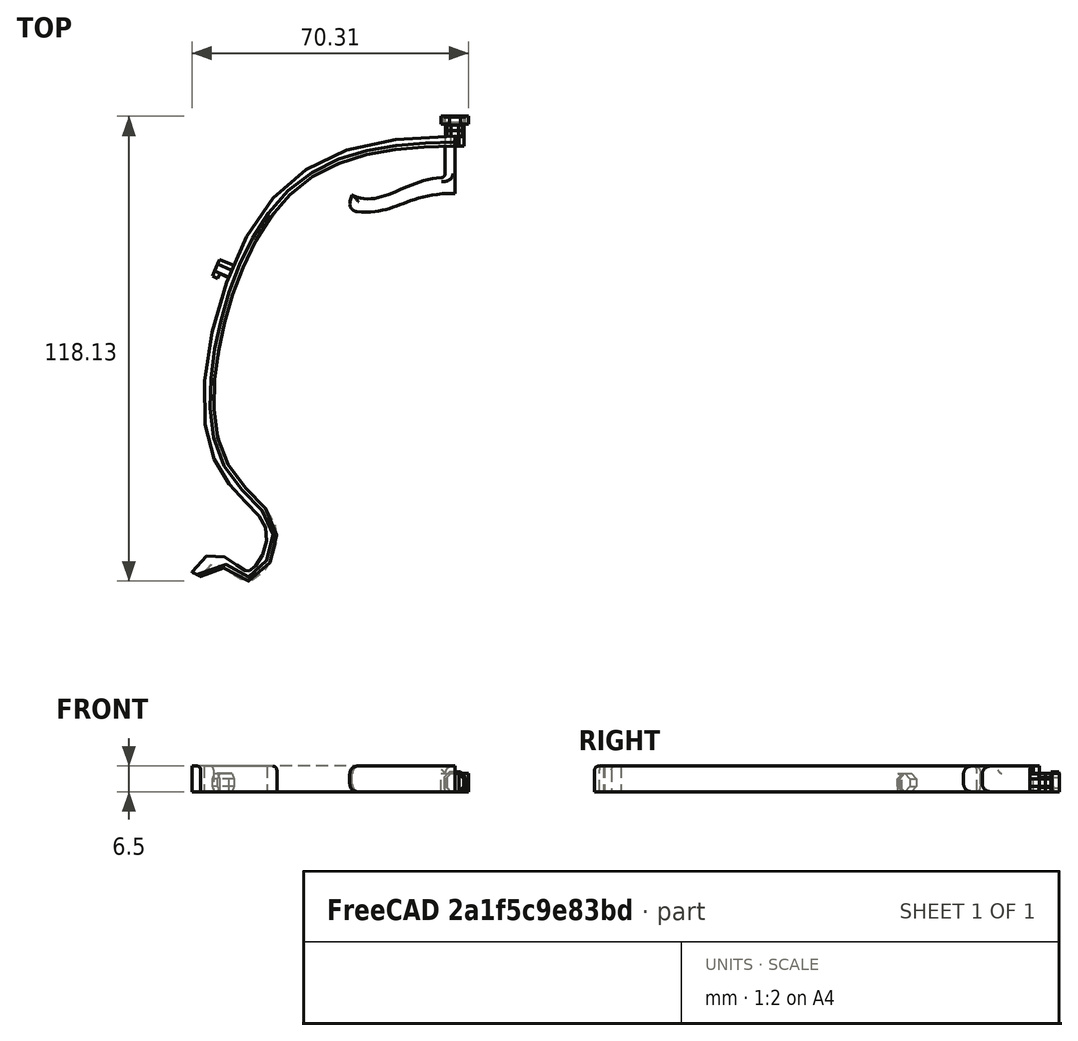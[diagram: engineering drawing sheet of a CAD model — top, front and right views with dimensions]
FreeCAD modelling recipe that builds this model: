
FCSTD DOCUMENT  (FreeCAD 0.18R16146 (Git))
Label: frame-001-02
License: All rights reserved
LicenseURL: http://ja.wikipedia.org/wiki/%E8%91%97%E4%BD%9C%E6%A8%A9%E8%A1%A8%E7%A4%BA
objects: Sketcher::SketchObject×5, Part::Extrusion×5, Part::Box×3, Part::Cut×2, Part::Fillet×2, Part::Compound×2, Mesh::Feature×1, Part::Sweep×1, Part::Mirroring×1, Part::MultiCommon×1
note: 22 computed .brp shape members not serialized (recipe doc carries the construction recipe); baked Part::Feature solids carry a one-line shape summary decoded from their .brp

FEATURE [Sketcher::SketchObject] Sketch  label="Sketch_FrameShape"
  sketch-geometry (15):
    g0-g7: Circle [constr] x8 (B-spline internal-alignment scaffolding for g8; pole/knot coordinates omitted)
    g8: BSplineCurve PolesCount=8 KnotsCount=6 Degree=3 IsPeriodic=0
    g9-g14: GeomPoint [constr] x6 (B-spline internal-alignment scaffolding for g8; pole/knot coordinates omitted)
  constraints (6):
    c: Radius(g0) = 6
    c: Equal(g0, g1-g6) x6
    c: InternalAlignment(g0-g7 -> g8) x8
    c: InternalAlignment(g9-g14 -> g8) x6
    c: Horizontal(g1,g8)
    c: Coincident(g-1,g8)
FEATURE [Sketcher::SketchObject] Sketch001
  Placement = pos=(0,0,0) rot=(0.57735,0.57735,0.57735;2.0944rad)
  sketch-geometry (4):
    g0: LineSegment StartX=0 StartY=6.5 StartZ=0 EndX=2.5 EndY=6.5 EndZ=0
    g1: LineSegment StartX=2.5 StartY=6.5 StartZ=0 EndX=2.5 EndY=0 EndZ=0
    g2: LineSegment StartX=2.5 StartY=0 StartZ=0 EndX=0 EndY=0 EndZ=0
    g3: LineSegment StartX=0 StartY=0 StartZ=0 EndX=0 EndY=6.5 EndZ=0
  constraints (12):
    c: Coincident(g0,g1)
    c: Coincident(g1,g2)
    c: Coincident(g2,g3)
    c: Coincident(g3,g0)
    c: Horizontal(g0)
    c: Horizontal(g2)
    c: Vertical(g1)
    c: Vertical(g3)
    c: DistanceX(g0,g0) = 2.5
    c: DistanceY(g1,g0) = 6.5
    c: DistanceX(g-1,g2) = 0
    c: PointOnObject(g2,g-1)
FEATURE [Mesh::Feature] cd43cbcc_75a4_11ea_893f_42010a00001e_UM3E_Visor_frame_EUROPE_ISO838_v3  label="cd43cbcc-75a4-11ea-893f-42010a00001e_UM3E_Visor_frame_EUROPE_ISO838_v3"
  Placement = pos=(0,-59,0) rot=(0,0,1;0rad)
FEATURE [Sketcher::SketchObject] Sketch002  label="OctPinSketch"
  Placement = pos=(0,0,0) rot=(1,0,0;1.5708rad)
  sketch-geometry (9):
    g0: LineSegment StartX=2.3097 StartY=1.35299 StartZ=0 EndX=2.3097 EndY=3.26641 EndZ=0
    g1: LineSegment StartX=2.3097 StartY=3.26641 StartZ=0 EndX=0.956709 EndY=4.6194 EndZ=0
    g2: LineSegment StartX=0.956709 StartY=4.6194 StartZ=0 EndX=-0.956709 EndY=4.6194 EndZ=0
    g3: LineSegment StartX=-0.956709 StartY=4.6194 StartZ=0 EndX=-2.3097 EndY=3.26641 EndZ=0
    g4: LineSegment StartX=-2.3097 StartY=3.26641 StartZ=0 EndX=-2.3097 EndY=1.35299 EndZ=0
    g5: LineSegment StartX=-2.3097 StartY=1.35299 StartZ=0 EndX=-0.956709 EndY=0 EndZ=0
    g6: LineSegment StartX=-0.956709 StartY=0 StartZ=0 EndX=0.956709 EndY=0 EndZ=0
    g7: LineSegment StartX=0.956709 StartY=0 StartZ=0 EndX=2.3097 EndY=1.35299 EndZ=0
    g8: Circle [constr] CenterX=0 CenterY=2.3097 CenterZ=0 NormalX=0 NormalY=0 NormalZ=1 AngleXU=0 Radius=2.5
  constraints (21):
    c: Coincident(g0,g1)
    c: Coincident(g1,g2)
    c: Coincident(g2,g3)
    c: Coincident(g3,g4)
    c: Coincident(g4,g5)
    c: Coincident(g5,g6)
    c: Coincident(g6,g7)
    c: Coincident(g7,g0)
    c: Equal(g0, g1-g7) x7
    c: PointOnObject(g0,g8)
    c: PointOnObject(g1,g8)
    c: PointOnObject(g2,g8)
    c: PointOnObject(g3,g8)
    c: PointOnObject(g4,g8)
    c: PointOnObject(g5,g8)
    c: PointOnObject(g6,g8)
    c: PointOnObject(g7,g8)
    c: Distance(g0,g8) = 2.5
    c: Horizontal(g6)
    c: PointOnObject(g8,g-2)
    c: PointOnObject(g6,g-1)
FEATURE [Part::Extrusion] Extrude002  label="OctPin"
  Base = -> Sketch002
  Dir = (0,-1,0)
  DirMode = 2
  FaceMakerClass = Part::FaceMakerBullseye
  LengthFwd = -6
  LengthRev = 0
  Solid = true
  Symmetric = false
FEATURE [Part::Extrusion] Extrude003  label="OctPinFront"
  Base = -> Sketch002
  Dir = (0,-1,2e-16)
  DirMode = 2
  FaceMakerClass = Part::FaceMakerBullseye
  LengthFwd = -3
  LengthRev = 0
  Placement = pos=(0,3,0) rot=(0,0,1;0rad)
  Solid = true
  Symmetric = false
FEATURE [Part::Extrusion] Extrude004  label="OctPin_WNotch_column"
  Base = -> Sketch002
  Dir = (0,-1,2e-16)
  DirMode = 2
  FaceMakerClass = Part::FaceMakerBullseye
  LengthFwd = -4
  LengthRev = 0
  Solid = true
  Symmetric = false
FEATURE [Part::Box] Box008  label="立方体008"
  AttacherType = Attacher::AttachEngine3D
  Height = 6
  Length = 2
  Placement = pos=(1,0,-0.5) rot=(0,0,1;0rad)
  Width = 2.5
FEATURE [Part::Cut] Cut  label="OctPin_WNotch"
  Base = -> Extrude004
  Tool = -> Box008
FEATURE [Part::Cut] Cut001  label="OctPin_WNotchR"
  Base = -> Extrude004
  Placement = pos=(57,-32.51,0) rot=(0,0,-1;1.15192rad)
  Tool = -> Box008
FEATURE [Sketcher::SketchObject] Sketch003
  sketch-geometry (18):
    g0: LineSegment StartX=0 StartY=1 StartZ=0 EndX=0 EndY=-12 EndZ=0
    g1: LineSegment StartX=2.5 StartY=-8 StartZ=0 EndX=2.5 EndY=1 EndZ=0
    g2: LineSegment StartX=2.5 StartY=1 StartZ=0 EndX=0 EndY=1 EndZ=0
    g3: LineSegment StartX=26.0622 StartY=-12.5 StartZ=0 EndX=27.3506 EndY=-16.2868 EndZ=0
    g4-g7: Circle [constr] x4 (B-spline internal-alignment scaffolding for g8; pole/knot coordinates omitted)
    g8: BSplineCurve PolesCount=4 KnotsCount=2 Degree=3 IsPeriodic=0
    g9: GeomPoint [constr] X=2.5 Y=-8 Z=0
    g10: GeomPoint [constr] X=26.0622 Y=-12.5 Z=0
    g11-g14: Circle [constr] x4 (B-spline internal-alignment scaffolding for g15; pole/knot coordinates omitted)
    g15: BSplineCurve PolesCount=4 KnotsCount=2 Degree=3 IsPeriodic=0
    g16: GeomPoint [constr] X=0 Y=-12 Z=0
    g17: GeomPoint [constr] X=27.3506 Y=-16.2868 Z=0
  constraints (32):
    c: PointOnObject(g0,g-2)
    c: Vertical(g0)
    c: Vertical(g1)
    c: Coincident(g1,g2)
    c: Coincident(g2,g0)
    c: DistanceX(g0,g1) = 2.5
    c: Horizontal(g2)
    c: DistanceY(g-1,g0) = 1
    c: DistanceY(g3,g1) = 4.5
    c: DistanceY(g0,g1) = 4
    c: DistanceY(g0,g-1) = 12
    c: Coincident(g8,g1)
    c: Radius(g4) = 2
    c: Equal(g4,g5)
    c: Equal(g4,g6)
    c: Equal(g4,g7)
    c: Coincident(g8,g3)
    c: InternalAlignment(g4-g7 -> g8) x4
    c: InternalAlignment(g9,g8)
    c: InternalAlignment(g10,g8)
    c: Coincident(g15,g0)
    c: Radius(g11) = 2
    c: Equal(g11,g12)
    c: Equal(g11,g13)
    c: Equal(g11,g14)
    c: Coincident(g15,g3)
    c: InternalAlignment(g11-g14 -> g15) x4
    c: InternalAlignment(g16,g15)
    c: InternalAlignment(g17,g15)
    c: Distance(g3,g3) = 4
    c: Horizontal(g0,g12)
    c: Horizontal(g5,g1)
FEATURE [Part::Extrusion] Extrude
  Base = -> Sketch003
  Dir = (0,0,1)
  DirMode = 2
  FaceMakerClass = Part::FaceMakerBullseye
  LengthFwd = 6.5
  LengthRev = 0
  Solid = true
  Symmetric = false
FEATURE [Part::Fillet] Fillet  label="AGOATE_R"
  Base = -> Extrude
  Edges = 8 edges: [Edge1 r=1,Edge4 r=2,Edge11 r=2,Edge12 r=2,Edge13 r=2,Edge15 r=2,Edge16 r=2,Edge18 r=1]
FEATURE [Part::Sweep] Sweep  label="Sweep_RightFrame"
  Frenet = false
  Sections = -> [Sketch001]
  Solid = true
  Spine = -> Sketch [Edge1]
  Transition = 1
FEATURE [Part::Fillet] Fillet001  label="Fillet_Sweep_RightFrame"
  Base = -> Sweep
  Edges = 1 edges r=1: [Edge1]
FEATURE [Part::Compound] Compound  label="RightSide"
  Links = -> [Cut001,Fillet,Fillet001]
FEATURE [Part::Mirroring] Part__Mirroring001  label="LeftSide (Mirrored)"
  Base = (0,0,0)
  Normal = (1,0,0)
  Source = -> Compound
FEATURE [Part::Box] Box  label="立方体"
  AttacherType = Attacher::AttachEngine3D
  Height = 10
  Length = 4
  Placement = pos=(-2,2.8,0) rot=(0,0,1;0rad)
  Width = 4
FEATURE [Part::Box] Box010  label="立方体010"
  AttacherType = Attacher::AttachEngine3D
  Height = 4.7
  Length = 7
  Placement = pos=(-3.5,5.6,0) rot=(0,0,1;0rad)
  Width = 2
FEATURE [Part::MultiCommon] Common  label="前ダボ柱"
  Shapes = -> [Extrude003,Box]
FEATURE [Sketcher::SketchObject] Sketch004
  MapMode = 5
  Placement = pos=(0,6,0) rot=(0,0.707107,0.707107;3.14159rad)
  Support = -> [Common]
  sketch-geometry (8):
    g0: LineSegment StartX=-2.34451 StartY=0 StartZ=0 EndX=-2.75 EndY=1.00428 EndZ=0
    g1: LineSegment StartX=-2.75 StartY=1.00428 StartZ=0 EndX=-2.75 EndY=3.6504 EndZ=0
    g2: LineSegment StartX=-2.75 StartY=3.6504 StartZ=0 EndX=-1.4004 EndY=5 EndZ=0
    g3: LineSegment StartX=-1.4004 StartY=5 StartZ=0 EndX=1.4004 EndY=5 EndZ=0
    g4: LineSegment StartX=1.4004 StartY=5 StartZ=0 EndX=2.75 EndY=3.6504 EndZ=0
    g5: LineSegment StartX=2.75 StartY=3.6504 StartZ=0 EndX=2.75 EndY=1.00428 EndZ=0
    g6: LineSegment StartX=2.75 StartY=1.00428 StartZ=0 EndX=2.34451 EndY=0 EndZ=0
    g7: LineSegment StartX=2.34451 StartY=0 StartZ=0 EndX=-2.34451 EndY=0 EndZ=0
  constraints (17):
    c: Coincident(g0,g1)
    c: Coincident(g1,g2)
    c: Coincident(g2,g3)
    c: Coincident(g3,g4)
    c: Coincident(g4,g5)
    c: Coincident(g5,g6)
    c: Coincident(g6,g7)
    c: Coincident(g7,g0)
    c: Vertical(g1)
    c: Symmetric(g0,g6,g-2)
    c: Symmetric(g0,g5,g-2)
    c: Symmetric(g1,g4,g-2)
    c: Symmetric(g2,g3,g-2)
    c: PointOnObject(g6,g-1)
    c: DistanceY(g6,g3) = 5
    c: DistanceX(g0,g5) = 5.5
    c: Angle(g5,g4,g4) = 0.785398
FEATURE [Part::Extrusion] Extrude005  label="前ダボトメ"
  Base = -> Sketch004
  Dir = (0,1,-2e-16)
  DirMode = 2
  FaceMakerClass = Part::FaceMakerBullseye
  LengthFwd = 2
  LengthRev = 0
  Solid = true
  Symmetric = false
FEATURE [Part::Compound] Compound001  label="前ダボ"
  Links = -> [Common,Extrude005]
  Placement = pos=(0,-0.6,0) rot=(0,0,1;0rad)
